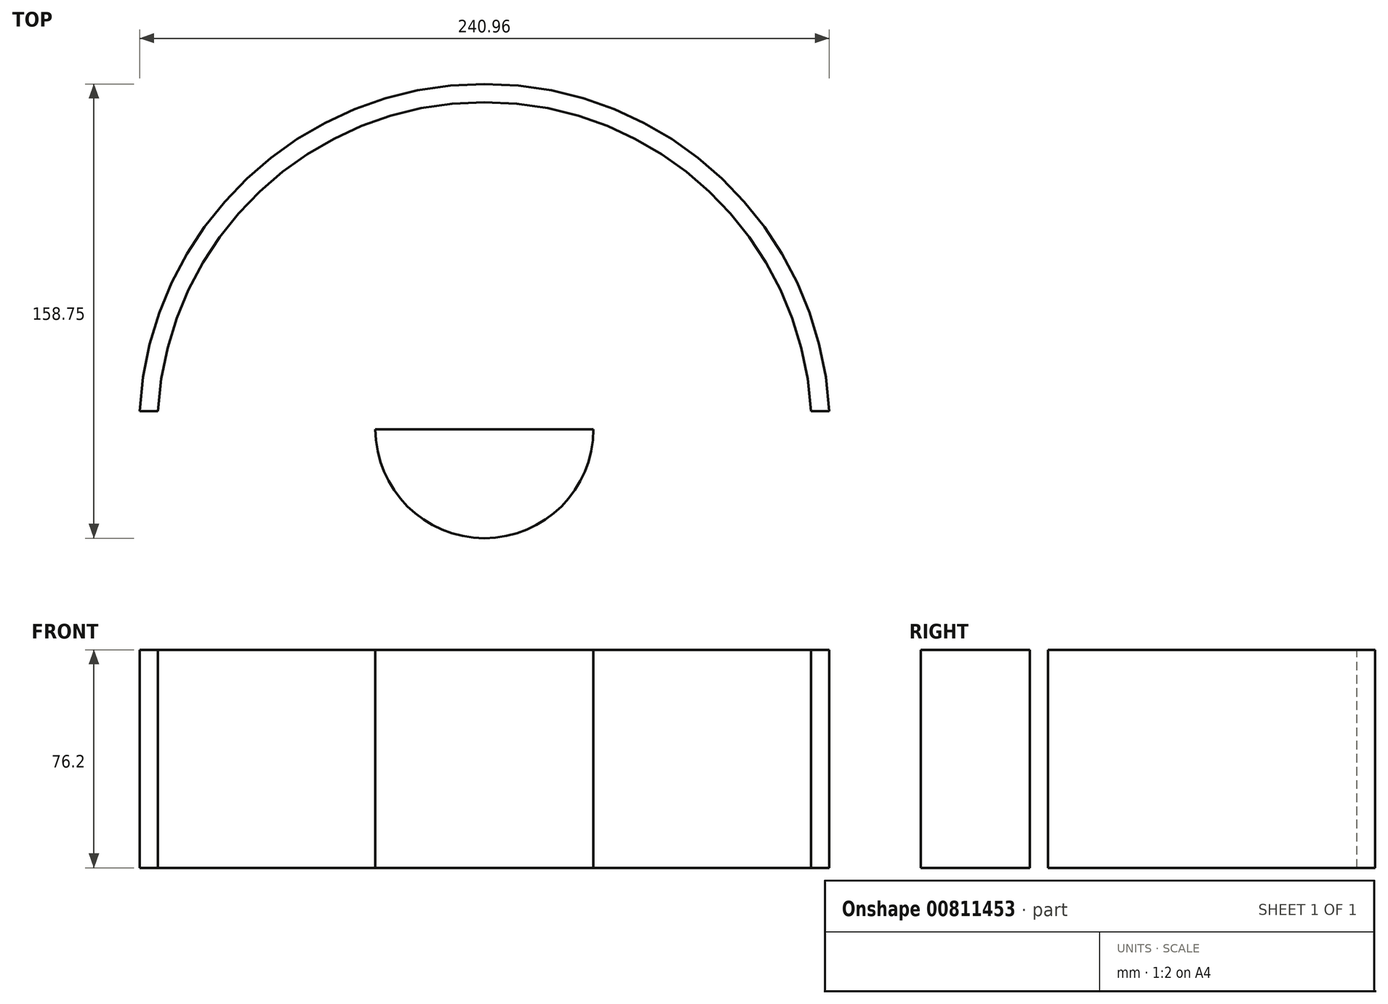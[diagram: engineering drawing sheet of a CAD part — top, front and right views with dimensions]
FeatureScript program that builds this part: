
annotation { "Feature Type Name" : "Feature", "Feature Type Description" : "" }
export const myFeature = defineFeature(function(context is Context, id is Id, definition is map)
    precondition{}
    {
        {
            var Q0;
            Q0=qCreatedBy(makeId("Top.planeOp"),FACE);
            var sketch = newSketch(context, id + "F0", { "sketchPlane" : qUnion([Q0])});
            skCircle(sketch, "E0", {"center": v(0, 0) * mm, "radius": 114.3 * mm});
            skLineSegment(sketch, "E1", {"start": v(0, 0) * mm, "end": v(114.3, 0) * mm});
            skLineSegment(sketch, "E2.1.0", {"start": v(0, 0) * mm, "end": v(57.15, 98.99) * mm});
            skLineSegment(sketch, "E2.2.0", {"start": v(0, 0) * mm, "end": v(-57.15, 98.99) * mm});
            skLineSegment(sketch, "E2.3.0", {"start": v(0, 0) * mm, "end": v(-114.3, 0) * mm});
            skLineSegment(sketch, "E2.4.0", {"start": v(0, 0) * mm, "end": v(-57.15, -98.99) * mm});
            skLineSegment(sketch, "E2.5.0", {"start": v(0, 0) * mm, "end": v(57.15, -98.99) * mm});
            skCircle(sketch, "E3", {"center": v(0, 0) * mm, "radius": 38.1 * mm});
            skLineSegment(sketch, "E4.0", {"start": v(0, 12.7) * mm, "end": v(-51.65, 102.16) * mm});
            skLineSegment(sketch, "E4.1", {"start": v(0, 12.7) * mm, "end": v(51.65, 102.16) * mm});
            skLineSegment(sketch, "E5.0", {"start": v(0, 6.35) * mm, "end": v(-120.48, 6.35) * mm});
            skLineSegment(sketch, "E6.0", {"start": v(0, 6.35) * mm, "end": v(120.48, 6.35) * mm});
            skCircle(sketch, "E7.0", {"center": v(0, 0) * mm, "radius": 120.65 * mm});
            skSolve(sketch);
        }
        {
            var Q0;
            {var subQ0=sQuery(id+"F0.wireOp",EDGE,"E0");var subQ4=makeQuery(id+"F0.imprint","INTERSECT",VERTEX,{"derivedFrom":[subQ0,sQuery(id+"F0.wireOp",EDGE,"E2.1.0")]});Q0=makeQuery(id+"F0.imprint","IMPRINT",FACE,{"disambiguationData":[TD([[makeQuery(id+"F0.imprint","IMPRINT",EDGE,{"disambiguationData":[TD([[subQ4,1.0]])],"derivedFrom":subQ0}),-1.0]])]});}
            extrude(context, id + "F1", {"entities" : qUnion([Q0]), "endBound" : BoundingType.SYMMETRIC, "oppositeDirection" : true, "depth" : 76.2 * mm, "offsetDistance" : 25.4 * mm});
        }
        {
            var Q0;
            {var subQ1=sQuery(id+"F0.wireOp",EDGE,"E2.4.0");var subQ3=sQuery(id+"F0.wireOp",EDGE,"E3");var subQ4=makeQuery(id+"F0.imprint","INTERSECT",VERTEX,{"derivedFrom":[subQ1,subQ3]});Q0=makeQuery(id+"F0.imprint","IMPRINT",FACE,{"disambiguationData":[TD([[makeQuery(id+"F0.imprint","IMPRINT",EDGE,{"disambiguationData":[TD([[subQ4,-1.0]])],"derivedFrom":subQ3}),1.0]])]});}
            var Q1;
            {var subQ1=sQuery(id+"F0.wireOp",EDGE,"E1");var subQ3=sQuery(id+"F0.wireOp",EDGE,"E3");var subQ4=makeQuery(id+"F0.imprint","INTERSECT",VERTEX,{"derivedFrom":[subQ1,subQ3]});Q1=makeQuery(id+"F0.imprint","IMPRINT",FACE,{"disambiguationData":[TD([[makeQuery(id+"F0.imprint","IMPRINT",EDGE,{"disambiguationData":[TD([[subQ4,1.0]])],"derivedFrom":subQ3}),1.0]])]});}
            var Q2;
            {var subQ1=sQuery(id+"F0.wireOp",EDGE,"E2.3.0");var subQ3=sQuery(id+"F0.wireOp",EDGE,"E3");var subQ4=makeQuery(id+"F0.imprint","INTERSECT",VERTEX,{"derivedFrom":[subQ1,subQ3]});Q2=makeQuery(id+"F0.imprint","IMPRINT",FACE,{"disambiguationData":[TD([[makeQuery(id+"F0.imprint","IMPRINT",EDGE,{"disambiguationData":[TD([[subQ4,-1.0]])],"derivedFrom":subQ3}),1.0]])]});}
            extrude(context, id + "F2", {"entities" : qUnion([Q0, Q1, Q2]), "endBound" : BoundingType.SYMMETRIC, "depth" : 76.2 * mm, "offsetDistance" : 25.4 * mm});
        }
    });
